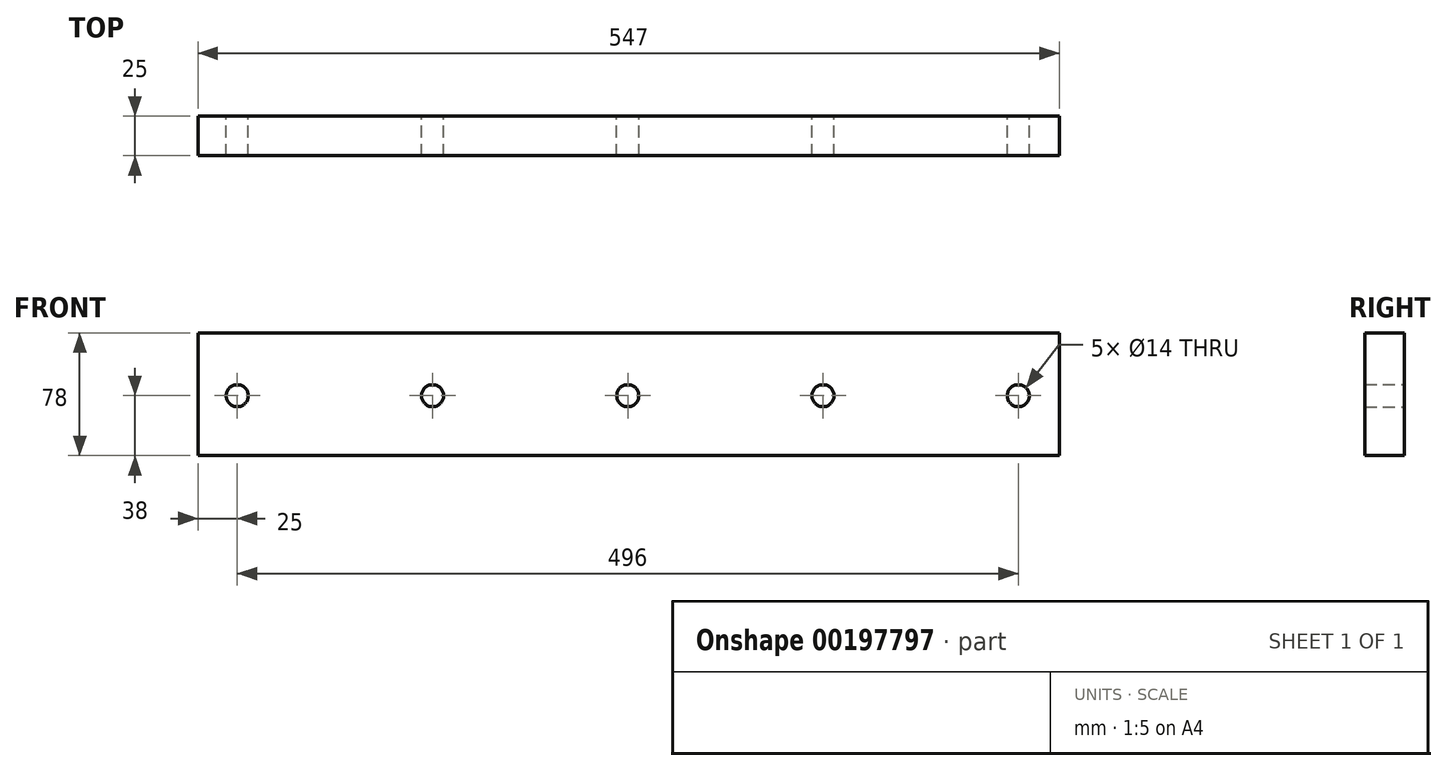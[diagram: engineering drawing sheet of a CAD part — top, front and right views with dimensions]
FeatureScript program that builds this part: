
annotation { "Feature Type Name" : "Feature", "Feature Type Description" : "" }
export const myFeature = defineFeature(function(context is Context, id is Id, definition is map)
    precondition{}
    {
        {
            var Q0;
            Q0=qCreatedBy(makeId("Front.planeOp"),FACE);
            var sketch = newSketch(context, id + "F0", { "sketchPlane" : qUnion([Q0])});
            skLineSegment(sketch, "E0.bottom", {"start": v(-273.5, 39) * mm, "end": v(273.5, 39) * mm});
            skLineSegment(sketch, "E0.top", {"start": v(-273.5, -39) * mm, "end": v(273.5, -39) * mm});
            skLineSegment(sketch, "E0.left", {"start": v(-273.5, 39) * mm, "end": v(-273.5, -39) * mm});
            skLineSegment(sketch, "E0.right", {"start": v(273.5, 39) * mm, "end": v(273.5, -39) * mm});
            skCircle(sketch, "E1", {"center": v(-248.5, -1) * mm, "radius": 7 * mm});
            skCircle(sketch, "E2", {"center": v(247.5, -1) * mm, "radius": 7 * mm});
            skPoint(sketch, "E3.endSnap0", {"position": v(273.5, 0) * mm});
            skCircle(sketch, "E4", {"center": v(-124.5, -1) * mm, "radius": 7 * mm});
            skCircle(sketch, "E5", {"center": v(-0.5, -1) * mm, "radius": 7 * mm});
            skCircle(sketch, "E6", {"center": v(123.5, -1) * mm, "radius": 7 * mm});
            skSolve(sketch);
        }
        {
            var Q0;
            Q0=makeQuery(id+"F0.imprint","IMPRINT",FACE,{"disambiguationData":[TD([[makeQuery(id+"F0.imprint","IMPRINT",EDGE,{"derivedFrom":sQuery(id+"F0.wireOp",EDGE,"E0.bottom")}),-1.0]])]});
            extrude(context, id + "F1", {"entities" : qUnion([Q0]), "endBound" : BoundingType.SYMMETRIC, "depth" : 25 * mm});
        }
    });
